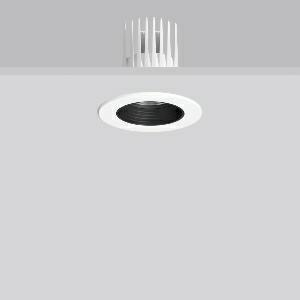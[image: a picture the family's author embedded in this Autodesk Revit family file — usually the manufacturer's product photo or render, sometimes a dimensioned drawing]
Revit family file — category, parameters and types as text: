
# Revit family: heledon_mini_e_901751_002_1_cd03
name_source: partatom
category: Lighting Fixtures
units: mm (PartAtom-declared; Revit-internal decimal feet)

## family parameters
Cut with Voids When Loaded = No
Host = Face
Light Source = No
Part Type = Normal
Room Calculation Point = No
Round Connector Dimension = Use Diameter
Shared = No

## types (1)
- HELEDON mini E (1 x LED Modul 940, 3400 lm, 4000)
    Apparent Load = 29 VA
    Approval mark = CE
    CIE Flux Codes = 99 100 100 100 100
    Color Rendering = 92
    Color Temperature = 4000
    Default Elevation = 1800 mm
    Description = Series: HELEDON mini
Round recessed downlight. Housing: die-cast aluminium, powder-coated. Black plastic ring and recessed LED to prevent glare from the side. Optical assembly with lens made of plastic (polycarbonate) for the best homogeneous light distribution - can be changed without tools. Best colour rendering index Ra>90. Suitable for Recessed ceiling mounting. Installation without tools thanks to spring fastening system. Including separate LED converter with connecting cable 600 mm.High quality converter without flickering and stroboscopic effect. Through-wiring box (5 pole) available as accessory. The following accessories can be mounted without use of tools: interchangeable lenses, decorative glasses, honeycomb louvre, clear and frosted diffusers, white interchangeable plastic ring. 
Colour: traffic white, matt (RAL 9016)
Diameter: 124 mm
Height: 3 mm
Cut-out diameter: 114 mm
Recess height: 170 mm
Luminaire: recess height: 120 mm
Lamp: LED
Socket: without socket
Colour temperature: 4000K
Colour rendering index (CRI): 92
System power: 29 W
Rated luminous flux: 3400 lm
Luminous efficiency: 117 lm/W
Control gear: Regulated power supply
Protection class: II
Type of protection: IP 20
    Height = 0 mm  [stored 0 ft]
    Lamp = 1 x LED Modul 940
    Lamp Light Flux = 3400 lm
    Lamp count = 1
    Length = 124 mm  [stored 0.406824 ft]
    Lifetime = 50000 h
    Luminous efficacy = 117 lm/W
    Manufacturer = RZB
    ModVariant = No
    Model = 901751.002.1
    Mounting Place = Ceiling
    Mounting Type = Recessed
    Number of Poles = 1
    OnlyDefault = Yes
    Power Factor = 1
    Product Name = HELEDON mini E
    Product group = Recessed downlights
    ProductGroupID = 402
    Protection Class = Protection class II
    Protection Degree = IP 20
    RLX_Detail_Level = 1
    RLX_Emergency_Light_Flux = 0 lm
    RLX_Emergency_Type = 0
    RLX_Emergency_Type_DB = No
    RlxData = <blob elided: 123393 chars, md5=d9772291>
    Socket = socket
    Standby Power = 0 W
    System Light Flux = 3400 lm
    System Power = 29 W
    Type Comments = Product without accessories
    Type Image = 901656.002.jpg
    URL = http://relux.com
    VarID = ---
    Voltage = 230 V
    Voltage Range = 220-240 V
    Weight = 0.00 kg
    Width = 0 mm  [stored 0 ft]

note: [stored X ft] marks values corroborated as IEEE doubles in the binary element streams (Revit-internal decimal feet)

## geometry (parser evidence)
native form markers: Blend x4, Sweep x10
no freeform markers — native parametric forms only
